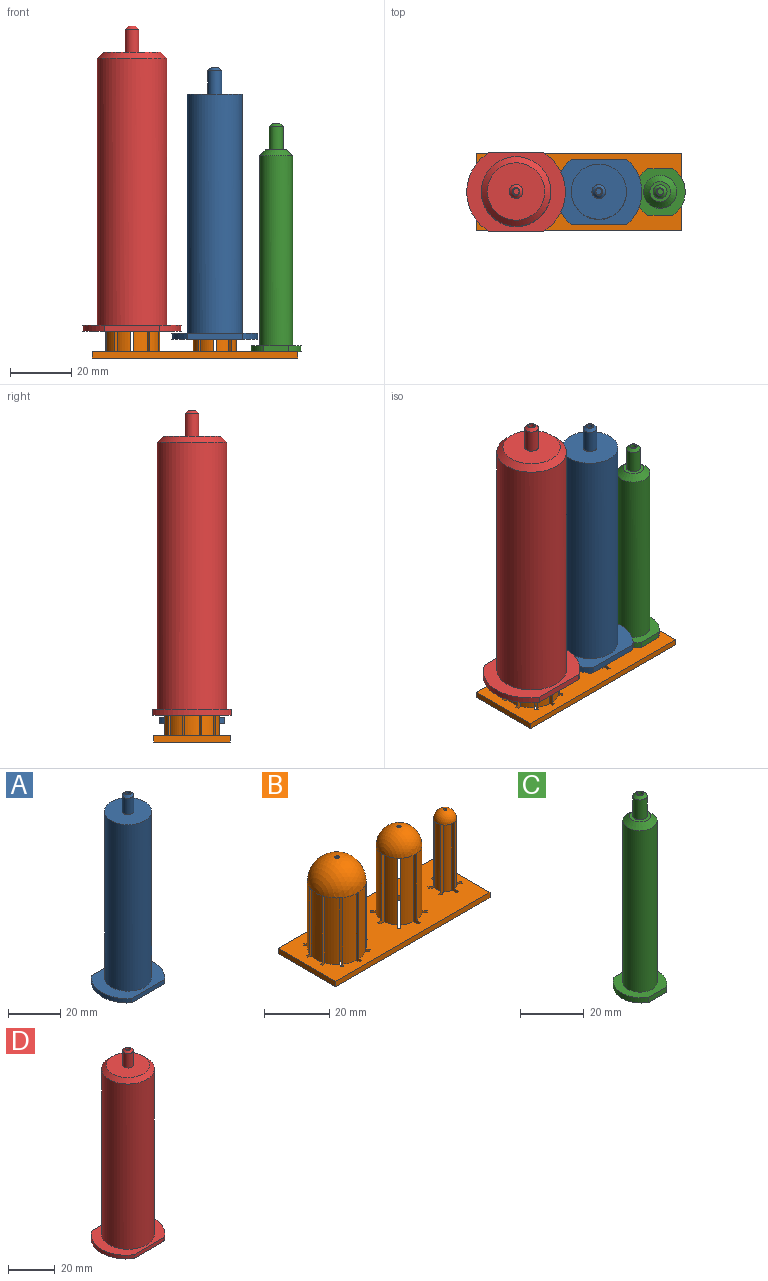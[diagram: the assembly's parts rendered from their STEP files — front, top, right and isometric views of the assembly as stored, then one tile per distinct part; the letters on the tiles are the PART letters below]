
ASSEMBLY  parts=4 mates=3
PART A: 15 faces, bbox 28.1x21.5x88.6 mm
  f0: cylinder r=9mm len=78mm, axis (0,0,-1), area 4410.8mm2, adj f1,f11
  f1: plane 18x18mm, normal (0,0,1), area 238.6mm2, adj f0,f3
  f2: cylinder r=1mm len=8.6mm, axis (0,0,-1), area 54mm2, adj f4,f5
  f3: cylinder r=2.25mm len=7.6mm, axis (0,0,-1), area 107.4mm2, adj f1,f6
  f4: plane 2.5x2.5mm, normal (0,0,1), area 1.8mm2, adj f2,f6
  f5: plane 2x2mm, normal (0,0,1), area 3.1mm2, adj f2
  f6: cone r=1.25mm half-angle=45deg, axis (0,0,-1), area 15.6mm2, adj f3,f4
  f7: plane 18x2mm, normal (0,1,0), area 36mm2, adj f8,f10,f11,f14
  f8: cylinder r=14mm len=21.5mm, axis (0,0,-1), area 49mm2, adj f7,f9,f11,f14
  f9: plane 18x2mm, normal (0,-1,0), area 36mm2, adj f8,f10,f11,f14
  f10: cylinder r=14mm len=21.5mm, axis (0,0,-1), area 49mm2, adj f7,f9,f11,f14
  f11: plane 28.06x21.5mm, normal (0,0,1), area 282.9mm2, adj f0,f7,f8,f9,f10
  f12: plane 15x15mm, normal (0,0,-1), area 176.7mm2, adj f13
  f13: cylinder r=7.5mm len=78mm, axis (0,0,-1), area 3675.7mm2, adj f12,f14
  f14: plane 28.06x21.5mm, normal (0,0,-1), area 360.7mm2, adj f7,f8,f9,f10,f13
PART B: 150 faces, bbox 67x25x36 mm
  f0: plane 67x25mm, normal (0,0,1), area 1190.2mm2, adj f2,f3,f4,f5,f6,f7,f8,f9
  f1: plane 67x25mm, normal (0,0,-1), area 1485.3mm2, adj f23,f24,f25,f26,f33,f34,f35,f36
  f2: cylinder r=9mm len=25mm, axis (0,0,-1), area 116.4mm2, adj f0,f30,f87,f88
  f3: cylinder r=9mm len=25mm, axis (0,0,-1), area 116.4mm2, adj f0,f30,f89,f90
  f4: cylinder r=9mm len=25mm, axis (0,0,-1), area 116.4mm2, adj f0,f30,f91,f92
  f5: cylinder r=9mm len=25mm, axis (0,0,-1), area 116.4mm2, adj f0,f30,f93,f94
  f6: cylinder r=9mm len=25mm, axis (0,0,-1), area 116.4mm2, adj f0,f30,f95,f96
  f7: cylinder r=9mm len=25mm, axis (0,0,-1), area 116.4mm2, adj f0,f30,f97,f98
  f8: cylinder r=9mm len=25mm, axis (0,0,-1), area 116.4mm2, adj f0,f30,f99,f100
  f9: cylinder r=9mm len=25mm, axis (0,0,-1), area 116.4mm2, adj f0,f30,f101,f102
  f10: cylinder r=9mm len=25mm, axis (0,0,-1), area 116.4mm2, adj f0,f30,f103,f104
  f11: cylinder r=7mm len=25mm, axis (0,0,-1), area 112.4mm2, adj f0,f31,f60,f61
  f12: cylinder r=7mm len=25mm, axis (0,0,-1), area 112.4mm2, adj f0,f31,f62,f63
  f13: cylinder r=7mm len=25mm, axis (0,0,-1), area 112.4mm2, adj f0,f31,f64,f65
  f14: cylinder r=7mm len=25mm, axis (0,0,-1), area 112.4mm2, adj f0,f31,f66,f67
  f15: cylinder r=7mm len=25mm, axis (0,0,-1), area 112.4mm2, adj f0,f31,f68,f69
  f16: cylinder r=7mm len=25mm, axis (0,0,-1), area 112.4mm2, adj f0,f31,f70,f71
  f17: cylinder r=7mm len=25mm, axis (0,0,-1), area 112.4mm2, adj f0,f31,f72,f73
  f18: cylinder r=3.5mm len=25mm, axis (0,0,-1), area 66.5mm2, adj f0,f32,f39,f40
  f19: cylinder r=3.5mm len=25mm, axis (0,0,-1), area 66.5mm2, adj f0,f32,f41,f42
  f20: cylinder r=3.5mm len=25mm, axis (0,0,-1), area 66.5mm2, adj f0,f32,f43,f44
  f21: cylinder r=3.5mm len=25mm, axis (0,0,-1), area 66.5mm2, adj f0,f32,f45,f46
  f22: cylinder r=3.5mm len=25mm, axis (0,0,-1), area 66.5mm2, adj f0,f32,f47,f48
  f23: plane 67x2mm, normal (0,1,0), area 134mm2, adj f0,f1,f24,f26
  f24: plane 25x2mm, normal (-1,0,0), area 50mm2, adj f0,f1,f23,f25
  f25: plane 67x2mm, normal (0,-1,0), area 134mm2, adj f0,f1,f24,f26
  f26: plane 25x2mm, normal (1,0,0), area 50mm2, adj f0,f1,f23,f25
  f27: cylinder r=9mm len=25mm, axis (0,0,-1), area 116.4mm2, adj f0,f30,f105,f106
  f28: cylinder r=7mm len=25mm, axis (0,0,-1), area 112.4mm2, adj f0,f31,f74,f75
  f29: cylinder r=3.5mm len=25mm, axis (0,0,-1), area 66.5mm2, adj f0,f32,f49,f50
  f30: sphere r=9mm, area 507.3mm2, adj f2,f3,f4,f5,f6,f7,f8,f9
  f31: sphere r=7mm, area 306.7mm2, adj f11,f12,f13,f14,f15,f16,f17,f28
  f32: sphere r=3.5mm, area 76.1mm2, adj f18,f19,f20,f21,f22,f29,f51,f144
  f33: plane 2x0.87mm, normal (0.87,-0.5,0), area 2mm2, adj f0,f1,f40,f41
  f34: plane 2x0.87mm, normal (0.87,0.5,0), area 2mm2, adj f0,f1,f42,f43
  f35: plane 2x1mm, normal (0,1,0), area 2mm2, adj f0,f1,f44,f45
  f36: plane 2x0.87mm, normal (-0.87,0.5,0), area 2mm2, adj f0,f1,f46,f47
  f37: plane 2x0.87mm, normal (-0.87,-0.5,0), area 2mm2, adj f0,f1,f48,f49
  f38: plane 2x1mm, normal (0,-1,0), area 2mm2, adj f0,f1,f39,f50
  f39: plane 27x4.47mm, normal (1,0,0), area 73.9mm2, adj f0,f1,f18,f38,f40,f51
  f40: plane 27x3.87mm, normal (-0.5,-0.87,0), area 73.9mm2, adj f0,f1,f18,f33,f39,f51
  f41: plane 27x3.87mm, normal (0.5,0.87,0), area 73.9mm2, adj f0,f1,f19,f33,f42,f51
  f42: plane 27x3.87mm, normal (0.5,-0.87,0), area 73.9mm2, adj f0,f1,f19,f34,f41,f51
  f43: plane 27x3.87mm, normal (-0.5,0.87,0), area 73.9mm2, adj f0,f1,f20,f34,f44,f51
  f44: plane 27x4.47mm, normal (1,0,0), area 73.9mm2, adj f0,f1,f20,f35,f43,f51
  f45: plane 27x4.47mm, normal (-1,0,0), area 73.9mm2, adj f0,f1,f21,f35,f46,f51
  f46: plane 27x3.87mm, normal (0.5,0.87,0), area 73.9mm2, adj f0,f1,f21,f36,f45,f51
  f47: plane 27x3.87mm, normal (-0.5,-0.87,0), area 73.9mm2, adj f0,f1,f22,f36,f48,f51
  f48: plane 27x3.87mm, normal (-0.5,0.87,0), area 73.9mm2, adj f0,f1,f22,f37,f47,f51
  f49: plane 27x3.87mm, normal (0.5,-0.87,0), area 73.9mm2, adj f0,f1,f29,f37,f50,f51
  f50: plane 27x4.47mm, normal (-1,0,0), area 73.9mm2, adj f0,f1,f29,f38,f49,f51
  f51: plane 7x6.5mm, normal (0,0,-1), area 17.5mm2, adj f32,f39,f40,f41,f42,f43,f44,f45
  f52: plane 2x0.71mm, normal (-0.71,0.71,0), area 2mm2, adj f0,f1,f61,f62
  f53: plane 2x1mm, normal (-1,0,0), area 2mm2, adj f0,f1,f63,f64
  f54: plane 2x0.71mm, normal (-0.71,-0.71,0), area 2mm2, adj f0,f1,f65,f66
  f55: plane 2x1mm, normal (0,-1,0), area 2mm2, adj f0,f1,f67,f68
  f56: plane 2x0.71mm, normal (0.71,-0.71,0), area 2mm2, adj f0,f1,f69,f70
  f57: plane 2x1mm, normal (1,0,0), area 2mm2, adj f0,f1,f71,f72
  f58: plane 2x0.71mm, normal (0.71,0.71,0), area 2mm2, adj f0,f1,f73,f74
  f59: plane 2x1mm, normal (0,1,0), area 2mm2, adj f0,f1,f60,f75
  f60: plane 27x7.53mm, normal (-1,0,0), area 159.4mm2, adj f0,f1,f11,f59,f61,f76
  f61: plane 27x5.33mm, normal (0.71,0.71,0), area 159.4mm2, adj f0,f1,f11,f52,f60,f76
  f62: plane 27x5.33mm, normal (-0.71,-0.71,0), area 159.4mm2, adj f0,f1,f12,f52,f63,f76
  f63: plane 27x7.53mm, normal (0,1,0), area 159.4mm2, adj f0,f1,f12,f53,f62,f76
  f64: plane 27x7.53mm, normal (0,-1,0), area 159.4mm2, adj f0,f1,f13,f53,f65,f76
  f65: plane 27x5.33mm, normal (-0.71,0.71,0), area 159.4mm2, adj f0,f1,f13,f54,f64,f76
  f66: plane 27x5.33mm, normal (0.71,-0.71,0), area 159.4mm2, adj f0,f1,f14,f54,f67,f76
  f67: plane 27x7.53mm, normal (-1,0,0), area 159.4mm2, adj f0,f1,f14,f55,f66,f76
  f68: plane 27x7.53mm, normal (1,0,0), area 159.4mm2, adj f0,f1,f15,f55,f69,f76
  f69: plane 27x5.33mm, normal (-0.71,-0.71,0), area 159.4mm2, adj f0,f1,f15,f56,f68,f76
  f70: plane 27x5.33mm, normal (0.71,0.71,0), area 159.4mm2, adj f0,f1,f16,f56,f71,f76
  f71: plane 27x7.53mm, normal (0,-1,0), area 159.4mm2, adj f0,f1,f16,f57,f70,f76
  f72: plane 27x7.53mm, normal (0,1,0), area 159.4mm2, adj f0,f1,f17,f57,f73,f76
  f73: plane 27x5.33mm, normal (0.71,-0.71,0), area 159.4mm2, adj f0,f1,f17,f58,f72,f76
  f74: plane 27x5.33mm, normal (-0.71,0.71,0), area 159.4mm2, adj f0,f1,f28,f58,f75,f76
  f75: plane 27x7.53mm, normal (1,0,0), area 159.4mm2, adj f0,f1,f28,f59,f74,f76
  f76: plane 14x14mm, normal (0,0,-1), area 50mm2, adj f31,f60,f61,f62,f63,f64,f65,f66
  f77: plane 2x0.95mm, normal (0.95,0.31,0), area 2mm2, adj f0,f1,f88,f89
  f78: plane 2x0.81mm, normal (0.59,0.81,0), area 2mm2, adj f0,f1,f90,f91
  f79: plane 2x1mm, normal (0,1,0), area 2mm2, adj f0,f1,f92,f93
  f80: plane 2x0.81mm, normal (-0.59,0.81,0), area 2mm2, adj f0,f1,f94,f95
  f81: plane 2x0.95mm, normal (-0.95,0.31,0), area 2mm2, adj f0,f1,f96,f97
  f82: plane 2x0.95mm, normal (-0.95,-0.31,0), area 2mm2, adj f0,f1,f98,f99
  f83: plane 2x0.81mm, normal (-0.59,-0.81,0), area 2mm2, adj f0,f1,f100,f101
  f84: plane 2x1mm, normal (0,-1,0), area 2mm2, adj f0,f1,f102,f103
  f85: plane 2x0.81mm, normal (0.59,-0.81,0), area 2mm2, adj f0,f1,f104,f105
  f86: plane 2x0.95mm, normal (0.95,-0.31,0), area 2mm2, adj f0,f1,f87,f106
  f87: plane 27x8.32mm, normal (0.31,0.95,0), area 203.7mm2, adj f0,f1,f2,f86,f88,f107
  f88: plane 27x8.32mm, normal (0.31,-0.95,0), area 203.7mm2, adj f0,f1,f2,f77,f87,f107
  f89: plane 27x8.32mm, normal (-0.31,0.95,0), area 203.7mm2, adj f0,f1,f3,f77,f90,f107
  f90: plane 27x7.07mm, normal (0.81,-0.59,0), area 203.7mm2, adj f0,f1,f3,f78,f89,f107
  f91: plane 27x7.07mm, normal (-0.81,0.59,0), area 203.7mm2, adj f0,f1,f4,f78,f92,f107
  f92: plane 27x8.74mm, normal (1,0,0), area 203.7mm2, adj f0,f1,f4,f79,f91,f107
  f93: plane 27x8.74mm, normal (-1,0,0), area 203.7mm2, adj f0,f1,f5,f79,f94,f107
  f94: plane 27x7.07mm, normal (0.81,0.59,0), area 203.7mm2, adj f0,f1,f5,f80,f93,f107
  f95: plane 27x7.07mm, normal (-0.81,-0.59,0), area 203.7mm2, adj f0,f1,f6,f80,f96,f107
  f96: plane 27x8.32mm, normal (0.31,0.95,0), area 203.7mm2, adj f0,f1,f6,f81,f95,f107
  f97: plane 27x8.32mm, normal (-0.31,-0.95,0), area 203.7mm2, adj f0,f1,f7,f81,f98,f107
  f98: plane 27x8.32mm, normal (-0.31,0.95,0), area 203.7mm2, adj f0,f1,f7,f82,f97,f107
  f99: plane 27x8.32mm, normal (0.31,-0.95,0), area 203.7mm2, adj f0,f1,f8,f82,f100,f107
  f100: plane 27x7.07mm, normal (-0.81,0.59,0), area 203.7mm2, adj f0,f1,f8,f83,f99,f107
  f101: plane 27x7.07mm, normal (0.81,-0.59,0), area 203.7mm2, adj f0,f1,f9,f83,f102,f107
  f102: plane 27x8.74mm, normal (-1,0,0), area 203.7mm2, adj f0,f1,f9,f84,f101,f107
  f103: plane 27x8.74mm, normal (1,0,0), area 203.7mm2, adj f0,f1,f10,f84,f104,f107
  f104: plane 27x7.07mm, normal (-0.81,-0.59,0), area 203.7mm2, adj f0,f1,f10,f85,f103,f107
  f105: plane 27x7.07mm, normal (0.81,0.59,0), area 203.7mm2, adj f0,f1,f27,f85,f106,f107
  f106: plane 27x8.32mm, normal (-0.31,-0.95,0), area 203.7mm2, adj f0,f1,f27,f86,f105,f107
  f107: plane 18x17.4mm, normal (0,0,-1), area 80.6mm2, adj f30,f87,f88,f89,f90,f91,f92,f93
  f108: plane 8.98x0.31mm, normal (0.31,0.95,0), area 2.9mm2, adj f30,f107,f109,f127
  f109: plane 8.98x0.26mm, normal (-0.81,0.59,0), area 2.9mm2, adj f30,f107,f108,f110
  f110: plane 8.98x0.26mm, normal (0.81,0.59,0), area 2.9mm2, adj f30,f107,f109,f111
  f111: plane 8.98x0.31mm, normal (-0.31,0.95,0), area 2.9mm2, adj f30,f107,f110,f112
  f112: plane 8.98x0.33mm, normal (1,0,0), area 2.9mm2, adj f30,f107,f111,f113
  f113: plane 8.98x0.31mm, normal (0.31,0.95,0), area 2.9mm2, adj f30,f107,f112,f114
  f114: plane 8.98x0.26mm, normal (0.81,-0.59,0), area 2.9mm2, adj f30,f107,f113,f115
  f115: plane 8.98x0.26mm, normal (0.81,0.59,0), area 2.9mm2, adj f30,f107,f114,f116
  f116: plane 8.98x0.31mm, normal (0.31,-0.95,0), area 2.9mm2, adj f30,f107,f115,f117
  f117: plane 8.98x0.33mm, normal (1,0,0), area 2.9mm2, adj f30,f107,f116,f118
  f118: plane 8.98x0.31mm, normal (-0.31,-0.95,0), area 2.9mm2, adj f30,f107,f117,f119
  f119: plane 8.98x0.26mm, normal (0.81,-0.59,0), area 2.9mm2, adj f30,f107,f118,f120
  f120: plane 8.98x0.26mm, normal (-0.81,-0.59,0), area 2.9mm2, adj f30,f107,f119,f121
  f121: plane 8.98x0.31mm, normal (0.31,-0.95,0), area 2.9mm2, adj f30,f107,f120,f122
  f122: plane 8.98x0.33mm, normal (-1,0,0), area 2.9mm2, adj f30,f107,f121,f123
  f123: plane 8.98x0.31mm, normal (-0.31,-0.95,0), area 2.9mm2, adj f30,f107,f122,f124
  f124: plane 8.98x0.26mm, normal (-0.81,0.59,0), area 2.9mm2, adj f30,f107,f123,f125
  f125: plane 8.98x0.26mm, normal (-0.81,-0.59,0), area 2.9mm2, adj f30,f107,f124,f126
  f126: plane 8.98x0.31mm, normal (-0.31,0.95,0), area 2.9mm2, adj f30,f107,f125,f127
  f127: plane 8.98x0.33mm, normal (-1,0,0), area 2.9mm2, adj f30,f107,f108,f126
  f128: plane 6.98x0.21mm, normal (-0.71,0.71,0), area 2mm2, adj f31,f76,f129,f143
  f129: plane 6.98x0.29mm, normal (-1,0,0), area 2mm2, adj f31,f76,f128,f130
  f130: plane 6.98x0.29mm, normal (0,1,0), area 2mm2, adj f31,f76,f129,f131
  f131: plane 6.98x0.21mm, normal (-0.71,0.71,0), area 2mm2, adj f31,f76,f130,f132
  f132: plane 6.98x0.21mm, normal (0.71,0.71,0), area 2mm2, adj f31,f76,f131,f133
  f133: plane 6.98x0.29mm, normal (0,1,0), area 2mm2, adj f31,f76,f132,f134
  f134: plane 6.98x0.29mm, normal (1,0,0), area 2mm2, adj f31,f76,f133,f135
  f135: plane 6.98x0.21mm, normal (0.71,0.71,0), area 2mm2, adj f31,f76,f134,f136
  f136: plane 6.98x0.21mm, normal (0.71,-0.71,0), area 2mm2, adj f31,f76,f135,f137
  f137: plane 6.98x0.29mm, normal (1,0,0), area 2mm2, adj f31,f76,f136,f138
  f138: plane 6.98x0.29mm, normal (0,-1,0), area 2mm2, adj f31,f76,f137,f139
  f139: plane 6.98x0.21mm, normal (0.71,-0.71,0), area 2mm2, adj f31,f76,f138,f140
  f140: plane 6.98x0.21mm, normal (-0.71,-0.71,0), area 2mm2, adj f31,f76,f139,f141
  f141: plane 6.98x0.29mm, normal (0,-1,0), area 2mm2, adj f31,f76,f140,f142
  f142: plane 6.98x0.29mm, normal (-1,0,0), area 2mm2, adj f31,f76,f141,f143
  f143: plane 6.98x0.21mm, normal (-0.71,-0.71,0), area 2mm2, adj f31,f76,f128,f142
  f144: plane 3.47x0.5mm, normal (-0.5,0.87,0), area 2mm2, adj f32,f51,f145,f149
  f145: plane 3.47x0.5mm, normal (0.5,0.87,0), area 2mm2, adj f32,f51,f144,f146
  f146: plane 3.46x0.58mm, normal (1,0,0), area 2mm2, adj f32,f51,f145,f147
  f147: plane 3.47x0.5mm, normal (0.5,-0.87,0), area 2mm2, adj f32,f51,f146,f148
  f148: plane 3.47x0.5mm, normal (-0.5,-0.87,0), area 2mm2, adj f32,f51,f147,f149
  f149: plane 3.46x0.58mm, normal (-1,0,0), area 2mm2, adj f32,f51,f144,f148
PART C: 16 faces, bbox 16.4x15.2x74.6 mm
  f0: cylinder r=5.35mm len=62mm, axis (0,0,-1), area 2084.1mm2, adj f2,f12
  f1: plane 6.7x6.7mm, normal (0,0,1), area 19.4mm2, adj f2,f4
  f2: cone r=3.35mm half-angle=45deg, axis (0,0,-1), area 77.3mm2, adj f0,f1
  f3: cylinder r=1mm len=8.6mm, axis (0,0,-1), area 54mm2, adj f5,f6
  f4: cylinder r=2.25mm len=7.6mm, axis (0,0,-1), area 107.4mm2, adj f1,f7
  f5: plane 2.5x2.5mm, normal (0,0,1), area 1.8mm2, adj f3,f7
  f6: plane 2x2mm, normal (0,0,1), area 3.1mm2, adj f3
  f7: cone r=1.25mm half-angle=45deg, axis (0,0,-1), area 15.6mm2, adj f4,f5
  f8: plane 8x2mm, normal (0,1,0), area 16mm2, adj f9,f11,f12,f15
  f9: cylinder r=9mm len=15.2mm, axis (0,0,-1), area 36.2mm2, adj f8,f10,f12,f15
  f10: plane 8x2mm, normal (0,-1,0), area 16mm2, adj f9,f11,f12,f15
  f11: cylinder r=9mm len=15.2mm, axis (0,0,-1), area 36.2mm2, adj f8,f10,f12,f15
  f12: plane 16.36x15.2mm, normal (0,0,1), area 121.3mm2, adj f0,f8,f9,f10,f11
  f13: plane 8.6x8.6mm, normal (0,0,-1), area 58.1mm2, adj f14
  f14: cylinder r=4.3mm len=64mm, axis (0,0,-1), area 1729.1mm2, adj f13,f15
  f15: plane 16.36x15.2mm, normal (0,0,-1), area 153.1mm2, adj f8,f9,f10,f11,f14
PART D: 16 faces, bbox 32.2x25.5x99.6 mm
  f0: cylinder r=11.35mm len=87mm, axis (0,0,-1), area 6204.3mm2, adj f2,f12
  f1: plane 18.7x18.7mm, normal (0,0,1), area 258.7mm2, adj f2,f4
  f2: cone r=9.35mm half-angle=45deg, axis (0,0,-1), area 183.9mm2, adj f0,f1
  f3: cylinder r=1mm len=8.6mm, axis (0,0,-1), area 54mm2, adj f5,f6
  f4: cylinder r=2.25mm len=7.6mm, axis (0,0,-1), area 107.4mm2, adj f1,f7
  f5: plane 2.5x2.5mm, normal (0,0,1), area 1.8mm2, adj f3,f7
  f6: plane 2x2mm, normal (0,0,1), area 3.1mm2, adj f3
  f7: cone r=1.25mm half-angle=45deg, axis (0,0,-1), area 15.6mm2, adj f4,f5
  f8: plane 18x2mm, normal (0,1,0), area 36mm2, adj f9,f11,f12,f15
  f9: cylinder r=15mm len=25.5mm, axis (0,0,-1), area 61mm2, adj f8,f10,f12,f15
  f10: plane 18x2mm, normal (0,-1,0), area 36mm2, adj f9,f11,f12,f15
  f11: cylinder r=15mm len=25.5mm, axis (0,0,-1), area 61mm2, adj f8,f10,f12,f15
  f12: plane 32.2x25.5mm, normal (0,0,1), area 310mm2, adj f0,f8,f9,f10,f11
  f13: plane 19.6x19.6mm, normal (0,0,-1), area 301.7mm2, adj f14
  f14: cylinder r=9.8mm len=89mm, axis (0,0,-1), area 5480.2mm2, adj f13,f15
  f15: plane 32.2x25.5mm, normal (0,0,-1), area 413mm2, adj f8,f9,f10,f11,f14
PLACE A t=(33.14,12.59,2.38)mm
PLACE B t=(33.14,12.59,-3.7)mm fixed
PLACE C t=(53.14,12.59,-1.69)mm
PLACE D t=(6.14,12.59,5.02)mm
MATE slider D.f14 <-> B.f2  axis (0,0,-1) through (6.14,12.59,5.02)mm
MATE slider C.f14 <-> B.f18  axis (0,0,-1) through (53.14,12.59,-1.69)mm
MATE slider A.f13 <-> B.f11  axis (0,0,-1) through (33.14,12.59,2.38)mm
